# Revit family: Haworth_CandorModern_Chair_HalfBack
name_source: partatom
category: Furniture
revit_build: Autodesk Revit 2018 (Build: 20170223_1515(x64)
units: mm (PartAtom-declared; Revit-internal decimal feet)

## family parameters
Always vertical = Yes
Cut with Voids When Loaded = No
OmniClass Number = 23.40.70.14.64.11
OmniClass Title = Office Furniture
Room Calculation Point = No
Shared = No
Work Plane-Based = No

## types (1)
- SAS-22-A3A
    Actual Depth = 22 7/8"
    Actual Height = 32 143/256"
    Actual Width = 21"
    Assembly Code = E2020200
    Description = Haworth_Chair_Candor_Modern_HalfBack
    Glide Finish = Haworth _ Polymer _ Black
    Manufacturer = Haworth
    Model = SAS-22-A3A
    Revision Number = 1
    Size = Verify Final Dim. w/ Haworth
    Sustainability Info = http://www.haworth.com
    URL = http://www.haworth.com
    URL - Product = http://www.haworth.com
    Warranty = http://www.haworth.com

## geometry (parser evidence)
native form markers: Sweep x4
no freeform markers — native parametric forms only
